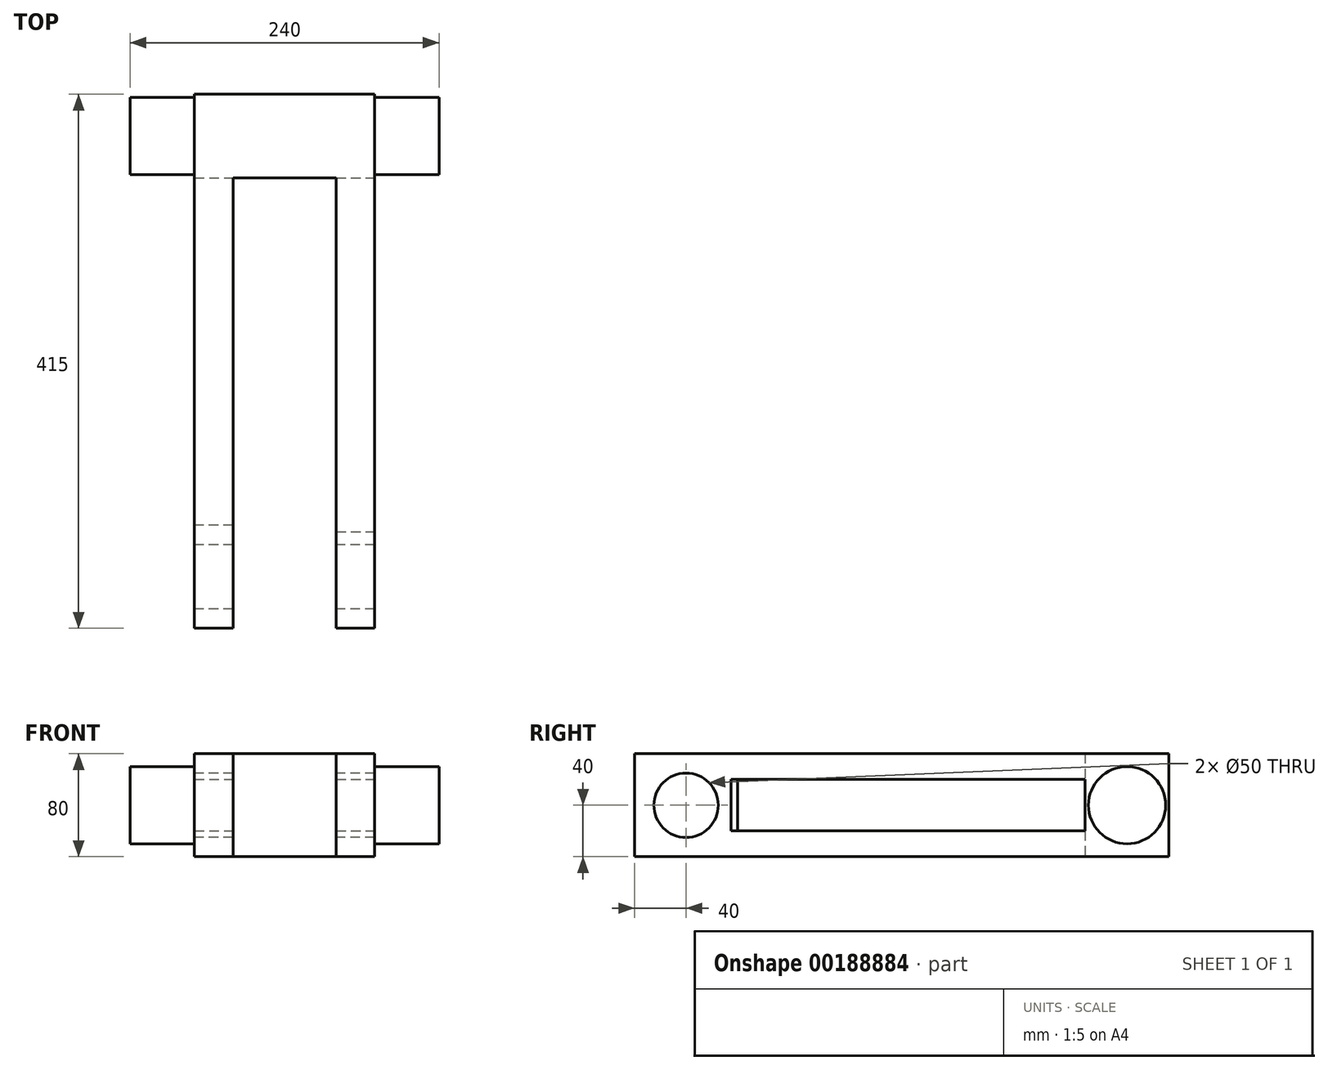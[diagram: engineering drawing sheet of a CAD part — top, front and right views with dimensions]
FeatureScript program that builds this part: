
annotation { "Feature Type Name" : "Feature", "Feature Type Description" : "" }
export const myFeature = defineFeature(function(context is Context, id is Id, definition is map)
    precondition{}
    {
        {
            var Q0;
            Q0=qCreatedBy(makeId("Right.planeOp"),FACE);
            var sketch = newSketch(context, id + "F0", { "sketchPlane" : qUnion([Q0])});
            skCircle(sketch, "E0", {"center": v(0, 0) * mm, "radius": 30 * mm});
            skSolve(sketch);
        }
        {
            var Q0;
            Q0=qSketchRegion(id+"F0",true);
            extrude(context, id + "F1", {"entities" : qUnion([Q0]), "depth" : 240 * mm});
        }
        {
            var Q0;
            Q0=qCreatedBy(makeId("Front.planeOp"),FACE);
            var sketch = newSketch(context, id + "F2", { "sketchPlane" : qUnion([Q0])});
            skLineSegment(sketch, "E1.bottom", {"start": v(50, 40) * mm, "end": v(190, 40) * mm});
            skLineSegment(sketch, "E1.top", {"start": v(50, -40) * mm, "end": v(190, -40) * mm});
            skLineSegment(sketch, "E1.left", {"start": v(50, 40) * mm, "end": v(50, -40) * mm});
            skLineSegment(sketch, "E1.right", {"start": v(190, 40) * mm, "end": v(190, -40) * mm});
            skSolve(sketch);
        }
        {
            var Q0;
            Q0=qSketchRegion(id+"F2",true);
            extrude(context, id + "F3", {"entities" : qUnion([Q0]), "operationType" : NewBodyOperationType.ADD, "depth" : (65 / 2) * mm, "hasSecondDirection" : true, "secondDirectionOppositeDirection" : true, "secondDirectionDepth" : 32.5 * mm});
        }
        {
            var Q0;
            Q0=makeQuery(id+"F3.opExtrude","CAP_FACE",FACE,{"disambiguationData":[OSD([sQuery(id+"F2.wireOp",EDGE,"E1.bottom"),sQuery(id+"F2.wireOp",EDGE,"E1.top"),sQuery(id+"F2.wireOp",EDGE,"E1.left"),sQuery(id+"F2.wireOp",EDGE,"E1.right")])],"isStart":false});
            var sketch = newSketch(context, id + "F4", { "sketchPlane" : qUnion([Q0])});
            skLineSegment(sketch, "E2.bottom", {"start": v(160, 40) * mm, "end": v(190, 40) * mm});
            skLineSegment(sketch, "E2.top", {"start": v(160, 20) * mm, "end": v(190, 20) * mm});
            skLineSegment(sketch, "E2.left", {"start": v(160, 40) * mm, "end": v(160, 20) * mm});
            skLineSegment(sketch, "E2.right", {"start": v(190, 40) * mm, "end": v(190, 20) * mm});
            skLineSegment(sketch, "E3.0.1.0", {"start": v(160, -20) * mm, "end": v(190, -20) * mm});
            skLineSegment(sketch, "E3.0.1.1", {"start": v(160, -40) * mm, "end": v(190, -40) * mm});
            skLineSegment(sketch, "E3.0.1.2", {"start": v(160, -20) * mm, "end": v(160, -40) * mm});
            skLineSegment(sketch, "E3.0.1.3", {"start": v(190, -20) * mm, "end": v(190, -40) * mm});
            skLineSegment(sketch, "E3.1.0.0", {"start": v(50, 40) * mm, "end": v(80, 40) * mm});
            skLineSegment(sketch, "E3.1.0.1", {"start": v(50, 20) * mm, "end": v(80, 20) * mm});
            skLineSegment(sketch, "E3.1.0.2", {"start": v(50, 40) * mm, "end": v(50, 20) * mm});
            skLineSegment(sketch, "E3.1.0.3", {"start": v(80, 40) * mm, "end": v(80, 20) * mm});
            skLineSegment(sketch, "E3.1.1.0", {"start": v(50, -20) * mm, "end": v(80, -20) * mm});
            skLineSegment(sketch, "E3.1.1.1", {"start": v(50, -40) * mm, "end": v(80, -40) * mm});
            skLineSegment(sketch, "E3.1.1.2", {"start": v(50, -20) * mm, "end": v(50, -40) * mm});
            skLineSegment(sketch, "E3.1.1.3", {"start": v(80, -20) * mm, "end": v(80, -40) * mm});
            skLineSegment(sketch, "E3.direction1", {"start": v(160, 20) * mm, "end": v(50, 20) * mm, "construction": true});
            skLineSegment(sketch, "E3.direction2", {"start": v(160, 20) * mm, "end": v(160, -40) * mm, "construction": true});
            skSolve(sketch);
        }
        {
            var Q0;
            Q0=qSketchRegion(id+"F4",true);
            extrude(context, id + "F5", {"entities" : qUnion([Q0]), "operationType" : NewBodyOperationType.ADD, "depth" : 350 * mm});
        }
        {
            var Q0;
            Q0=makeQuery(id+"F5.boolean.opBoolean","MERGE",FACE,{"derivedFrom":[makeQuery(id+"F3.opExtrude","SWEPT_FACE",FACE,{"disambiguationData":[OSD([sQuery(id+"F2.wireOp",EDGE,"E1.right")])]}),makeQuery(id+"F5.opExtrude","SWEPT_FACE",FACE,{"disambiguationData":[OSD([sQuery(id+"F4.wireOp",EDGE,"E2.right")])]}),makeQuery(id+"F5.opExtrude","SWEPT_FACE",FACE,{"disambiguationData":[OSD([sQuery(id+"F4.wireOp",EDGE,"E3.0.1.3")])]})]});
            var sketch = newSketch(context, id + "F6", { "sketchPlane" : qUnion([Q0])});
            skLineSegment(sketch, "E4.bottom", {"start": v(-382.5, 40) * mm, "end": v(-307.5, 40) * mm});
            skLineSegment(sketch, "E4.top", {"start": v(-382.5, -40) * mm, "end": v(-307.5, -40) * mm});
            skLineSegment(sketch, "E4.left", {"start": v(-382.5, 40) * mm, "end": v(-382.5, -40) * mm});
            skLineSegment(sketch, "E4.right", {"start": v(-307.5, 40) * mm, "end": v(-307.5, -40) * mm});
            skSolve(sketch);
        }
        {
            var Q0;
            Q0=qSketchRegion(id+"F6",true);
            extrude(context, id + "F7", {"entities" : qUnion([Q0]), "operationType" : NewBodyOperationType.ADD, "oppositeDirection" : true, "depth" : 30 * mm});
        }
        {
            var Q0;
            Q0=makeQuery(id+"F5.boolean.opBoolean","MERGE",FACE,{"derivedFrom":[makeQuery(id+"F3.opExtrude","SWEPT_FACE",FACE,{"disambiguationData":[OSD([sQuery(id+"F2.wireOp",EDGE,"E1.left")])]}),makeQuery(id+"F5.opExtrude","SWEPT_FACE",FACE,{"disambiguationData":[OSD([sQuery(id+"F4.wireOp",EDGE,"E3.1.0.2")])]}),makeQuery(id+"F5.opExtrude","SWEPT_FACE",FACE,{"disambiguationData":[OSD([sQuery(id+"F4.wireOp",EDGE,"E3.1.1.2")])]})]});
            var sketch = newSketch(context, id + "F8", { "sketchPlane" : qUnion([Q0])});
            skLineSegment(sketch, "E5.bottom", {"start": v(302.5, 40) * mm, "end": v(382.5, 40) * mm});
            skLineSegment(sketch, "E5.top", {"start": v(302.5, -40) * mm, "end": v(382.5, -40) * mm});
            skLineSegment(sketch, "E5.left", {"start": v(302.5, 40) * mm, "end": v(302.5, -40) * mm});
            skLineSegment(sketch, "E5.right", {"start": v(382.5, 40) * mm, "end": v(382.5, -40) * mm});
            skSolve(sketch);
        }
        {
            var Q0;
            Q0=qSketchRegion(id+"F8",true);
            extrude(context, id + "F9", {"entities" : qUnion([Q0]), "operationType" : NewBodyOperationType.ADD, "oppositeDirection" : true, "depth" : 30 * mm});
        }
        {
            var Q0;
            Q0=makeQuery(id+"F9.boolean.opBoolean","MERGE",FACE,{"derivedFrom":[makeQuery(id+"F5.boolean.opBoolean","MERGE",FACE,{"derivedFrom":[makeQuery(id+"F3.opExtrude","SWEPT_FACE",FACE,{"disambiguationData":[OSD([sQuery(id+"F2.wireOp",EDGE,"E1.left")])]}),makeQuery(id+"F5.opExtrude","SWEPT_FACE",FACE,{"disambiguationData":[OSD([sQuery(id+"F4.wireOp",EDGE,"E3.1.0.2")])]}),makeQuery(id+"F5.opExtrude","SWEPT_FACE",FACE,{"disambiguationData":[OSD([sQuery(id+"F4.wireOp",EDGE,"E3.1.1.2")])]})]}),makeQuery(id+"F9.opExtrude","CAP_FACE",FACE,{"disambiguationData":[OSD([sQuery(id+"F8.wireOp",EDGE,"E5.bottom"),sQuery(id+"F8.wireOp",EDGE,"E5.top"),sQuery(id+"F8.wireOp",EDGE,"E5.left"),sQuery(id+"F8.wireOp",EDGE,"E5.right")])],"isStart":true})]});
            var sketch = newSketch(context, id + "F10", { "sketchPlane" : qUnion([Q0])});
            skCircle(sketch, "E6", {"center": v(342.5, 0) * mm, "radius": 25 * mm});
            skSolve(sketch);
        }
        {
            var Q0;
            Q0=qSketchRegion(id+"F10",true);
            extrude(context, id + "F11", {"entities" : qUnion([Q0]), "operationType" : NewBodyOperationType.REMOVE, "endBound" : BoundingType.THROUGH_ALL, "oppositeDirection" : true, "depth" : 25 * mm});
        }
    });
